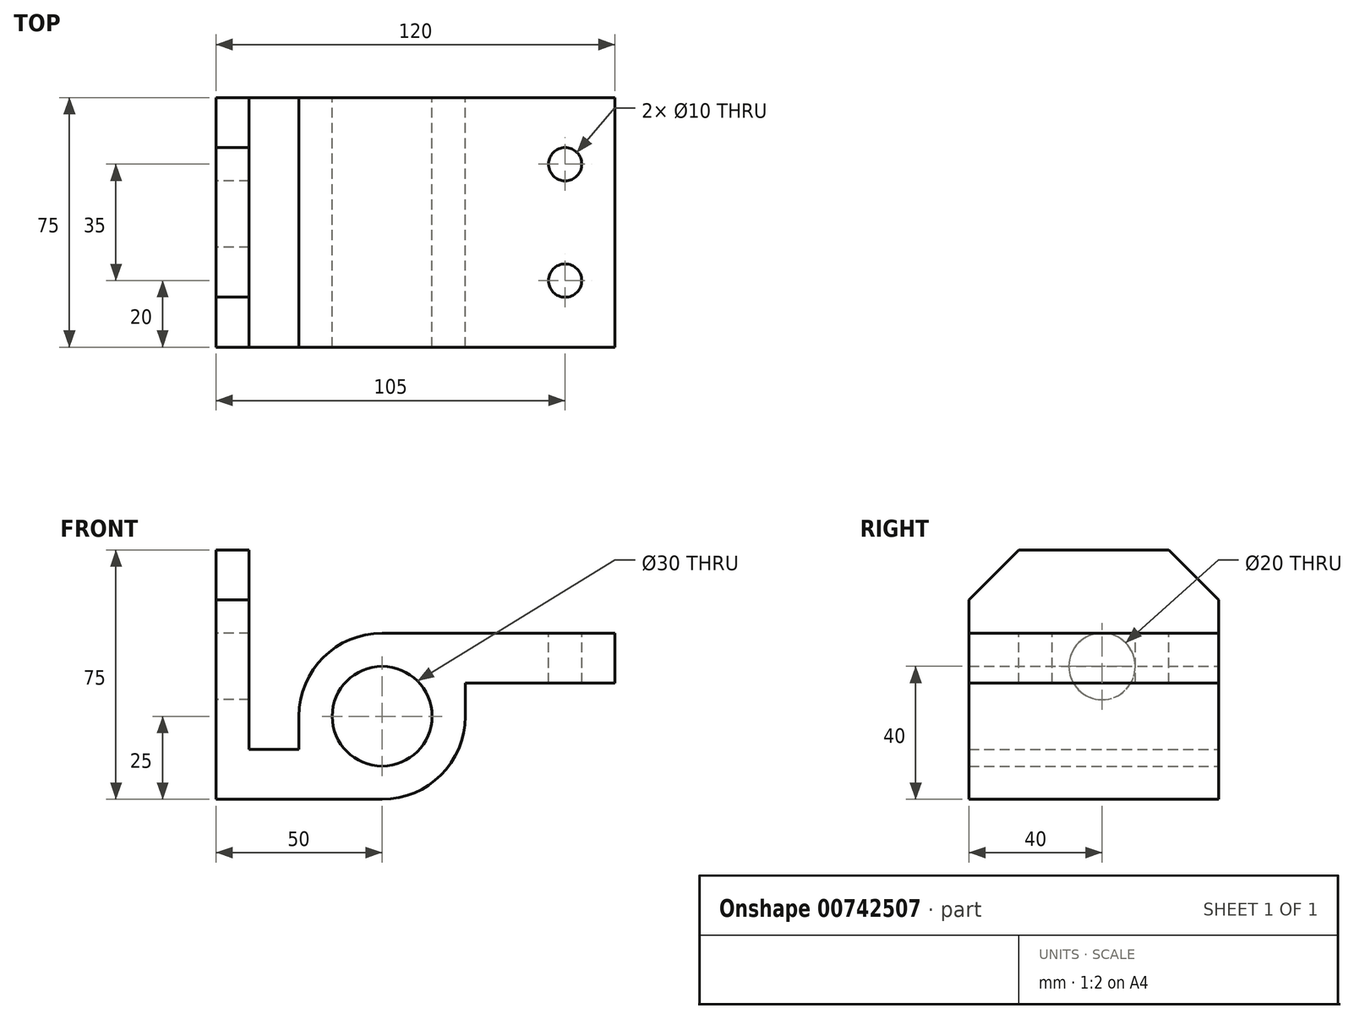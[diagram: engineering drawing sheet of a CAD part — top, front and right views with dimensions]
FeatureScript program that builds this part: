
annotation { "Feature Type Name" : "Feature", "Feature Type Description" : "" }
export const myFeature = defineFeature(function(context is Context, id is Id, definition is map)
    precondition{}
    {
        {
            var Q0;
            Q0=qCreatedBy(makeId("Front.planeOp"),FACE);
            var sketch = newSketch(context, id + "F0", { "sketchPlane" : qUnion([Q0])});
            skCircle(sketch, "E0", {"center": v(0, 0) * mm, "radius": 15 * mm});
            skArc(sketch, "E1", {"start": v(0, -25) * mm, "mid": v(17.68, -17.68) * mm, "end": v(25, 0) * mm});
            skLineSegment(sketch, "E2", {"start": v(0, -25) * mm, "end": v(-50, -25) * mm});
            skLineSegment(sketch, "E3", {"start": v(0, 25) * mm, "end": v(70, 25) * mm});
            skLineSegment(sketch, "E4", {"start": v(70, 25) * mm, "end": v(70, 10) * mm});
            skLineSegment(sketch, "E5", {"start": v(70, 10) * mm, "end": v(25, 10) * mm});
            skLineSegment(sketch, "E6", {"start": v(25, 0) * mm, "end": v(25, 10) * mm});
            skLineSegment(sketch, "E7", {"start": v(-50, -25) * mm, "end": v(-50, 50) * mm});
            skArc(sketch, "E8.trimOffspring", {"start": v(0, 25) * mm, "mid": v(-17.68, 17.68) * mm, "end": v(-25, 0) * mm});
            skLineSegment(sketch, "E9", {"start": v(-50, 50) * mm, "end": v(-40, 50) * mm});
            skLineSegment(sketch, "E10", {"start": v(-40, 50) * mm, "end": v(-40, -10) * mm});
            skLineSegment(sketch, "E11", {"start": v(-40, -10) * mm, "end": v(-25, -10) * mm});
            skLineSegment(sketch, "E12", {"start": v(-25, 0) * mm, "end": v(-25, -10) * mm});
            skSolve(sketch);
        }
        {
            var Q0;
            Q0 = qSketchRegion(id + "F0", true);
            var Q1;
            Q1=makeQuery(id+"F0.imprint","IMPRINT",FACE,{"disambiguationData":[TD([[makeQuery(id+"F0.imprint","IMPRINT",EDGE,{"derivedFrom":sQuery(id+"F0.wireOp",EDGE,"E0")}),-1.0]])]});
            extrude(context, id + "F1", {"entities" : qUnion([Q0, Q1]), "depth" : 75 * mm, "offsetDistance" : 25 * mm});
        }
        {
            var Q0;
            Q0=makeQuery(id+"F1.opExtrude","SWEPT_FACE",FACE,{"disambiguationData":[OSD([sQuery(id+"F0.wireOp",EDGE,"E7")])]});
            var sketch = newSketch(context, id + "F2", { "sketchPlane" : qUnion([Q0])});
            skLineSegment(sketch, "E13", {"start": v(0, 35) * mm, "end": v(15, 50) * mm});
            skLineSegment(sketch, "E14", {"start": v(60, 50) * mm, "end": v(75, 35) * mm});
            skPoint(sketch, "E15", {"position": v(35, 15) * mm});
            skCircle(sketch, "E16", {"center": v(35, 15) * mm, "radius": 10 * mm});
            skSolve(sketch);
        }
        {
            var Q0;
            Q0=makeQuery(id+"F2.imprint","IMPRINT",FACE,{"disambiguationData":[TD([[makeQuery(id+"F2.imprint","IMPRINT",EDGE,{"derivedFrom":sQuery(id+"F2.wireOp",EDGE,"E16")}),1.0]])]});
            var Q1;
            {var subQ0=sQuery(id+"F2.wireOp",EDGE,"E14");Q1=makeQuery(id+"F2.imprint","IMPRINT",FACE,{"disambiguationData":[TD([[makeQuery(id+"F2.imprint","IMPRINT",EDGE,{"derivedFrom":subQ0}),1.0]])]});}
            var Q2;
            {var subQ0=sQuery(id+"F2.wireOp",EDGE,"E13");Q2=makeQuery(id+"F2.imprint","IMPRINT",FACE,{"disambiguationData":[TD([[makeQuery(id+"F2.imprint","IMPRINT",EDGE,{"derivedFrom":subQ0}),1.0]])]});}
            extrude(context, id + "F3", {"entities" : qUnion([Q0, Q1, Q2]), "operationType" : NewBodyOperationType.REMOVE, "oppositeDirection" : true, "depth" : 18 * mm, "offsetDistance" : 25 * mm});
        }
        {
            var Q0;
            Q0=makeQuery(id+"F1.opExtrude","SWEPT_FACE",FACE,{"disambiguationData":[OSD([sQuery(id+"F0.wireOp",EDGE,"E3")])]});
            var sketch = newSketch(context, id + "F4", { "sketchPlane" : qUnion([Q0])});
            skCircle(sketch, "E17", {"center": v(55, -20) * mm, "radius": 5 * mm});
            skCircle(sketch, "E18", {"center": v(55, -55) * mm, "radius": 5 * mm});
            skSolve(sketch);
        }
        {
            var Q0;
            Q0=makeQuery(id+"F4.imprint","IMPRINT",FACE,{"disambiguationData":[TD([[makeQuery(id+"F4.imprint","IMPRINT",EDGE,{"derivedFrom":sQuery(id+"F4.wireOp",EDGE,"E17")}),1.0]])]});
            var Q1;
            Q1=makeQuery(id+"F4.imprint","IMPRINT",FACE,{"disambiguationData":[TD([[makeQuery(id+"F4.imprint","IMPRINT",EDGE,{"derivedFrom":sQuery(id+"F4.wireOp",EDGE,"E18")}),1.0]])]});
            extrude(context, id + "F5", {"entities" : qUnion([Q0, Q1]), "operationType" : NewBodyOperationType.REMOVE, "oppositeDirection" : true, "depth" : 25 * mm, "offsetDistance" : 25 * mm});
        }
    });
